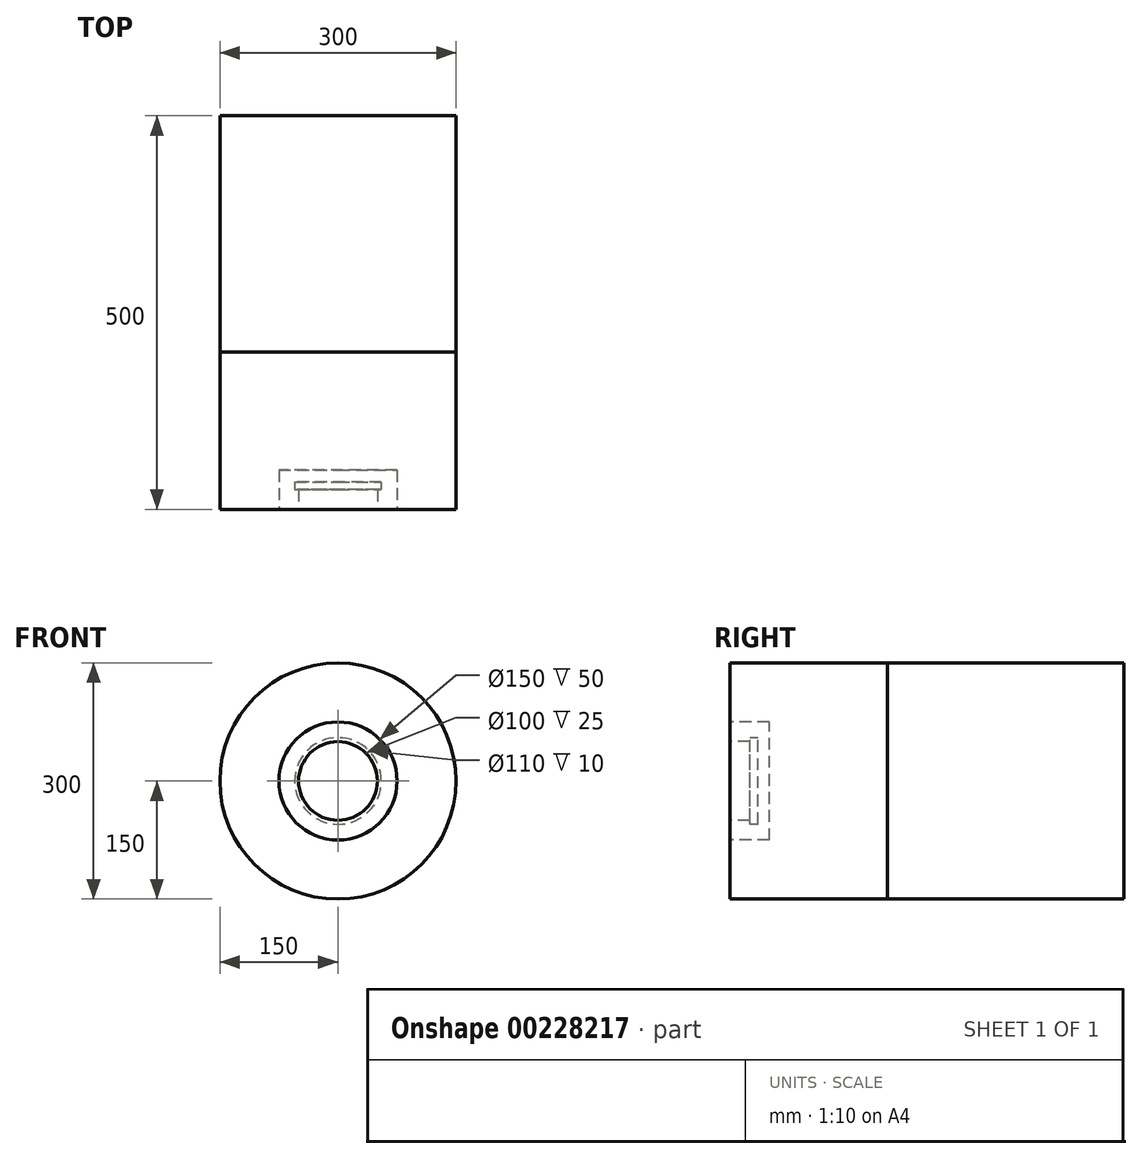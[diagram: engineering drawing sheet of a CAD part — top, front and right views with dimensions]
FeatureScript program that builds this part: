
annotation { "Feature Type Name" : "Feature", "Feature Type Description" : "" }
export const myFeature = defineFeature(function(context is Context, id is Id, definition is map)
    precondition{}
    {
        {
            var Q0;
            Q0=qCreatedBy(makeId("Front.planeOp"),FACE);
            var sketch = newSketch(context, id + "F0", { "sketchPlane" : qUnion([Q0])});
            skCircle(sketch, "E0", {"center": v(0, 0) * mm, "radius": 150 * mm});
            skSolve(sketch);
        }
        {
            var Q0;
            Q0=qCreatedBy(makeId("Front.planeOp"),FACE);
            var sketch = newSketch(context, id + "F1", { "sketchPlane" : qUnion([Q0])});
            skCircle(sketch, "E1", {"center": v(0, 0) * mm, "radius": 75 * mm});
            skSolve(sketch);
        }
        {
            var Q0;
            Q0=qCreatedBy(makeId("Front.planeOp"),FACE);
            var sketch = newSketch(context, id + "F2", { "sketchPlane" : qUnion([Q0])});
            skCircle(sketch, "E2", {"center": v(0, 0) * mm, "radius": 50 * mm});
            skSolve(sketch);
        }
        {
            var Q0;
            Q0 = qSketchRegion(id + "F0", true);
            extrude(context, id + "F3", {"entities" : qUnion([Q0]), "oppositeDirection" : true, "depth" : 200 * mm});
        }
        {
            var Q0;
            Q0=makeQuery(id+"F1.imprint","IMPRINT",FACE,{"disambiguationData":[TD([[makeQuery(id+"F1.imprint","IMPRINT",EDGE,{"derivedFrom":sQuery(id+"F1.wireOp",EDGE,"E1")}),1.0]])]});
            extrude(context, id + "F4", {"entities" : qUnion([Q0]), "operationType" : NewBodyOperationType.REMOVE, "oppositeDirection" : true, "depth" : 50 * mm});
        }
        {
            var Q0;
            Q0 = qSketchRegion(id + "F1", true);
            var Q1;
            Q1=makeQuery(id+"F4.boolean.opBoolean","COPY",FACE,{"derivedFrom":makeQuery(id+"F4.opExtrude","CAP_FACE",FACE,{"disambiguationData":[OSD([sQuery(id+"F1.wireOp",EDGE,"E1")])],"isStart":false})});
            extrude(context, id + "F5", {"entities" : qUnion([Q0]), "endBound" : BoundingType.UP_TO_SURFACE, "oppositeDirection" : true, "endBoundEntityFace" : qUnion([Q1]), "depth" : 25 * mm});
        }
        {
            var Q0;
            Q0 = qSketchRegion(id + "F2", true);
            extrude(context, id + "F6", {"entities" : qUnion([Q0]), "operationType" : NewBodyOperationType.REMOVE, "oppositeDirection" : true, "depth" : 25 * mm});
        }
        {
            var Q0;
            Q0=makeQuery(id+"F6.boolean.opBoolean","COPY",FACE,{"derivedFrom":makeQuery(id+"F6.opExtrude","CAP_FACE",FACE,{"disambiguationData":[OSD([sQuery(id+"F2.wireOp",EDGE,"E2")])],"isStart":false})});
            var sketch = newSketch(context, id + "F7", { "sketchPlane" : qUnion([Q0])});
            skCircle(sketch, "E3", {"center": v(0, 0) * mm, "radius": 55 * mm});
            skSolve(sketch);
        }
        {
            var Q0;
            Q0 = qSketchRegion(id + "F7", true);
            extrude(context, id + "F8", {"entities" : qUnion([Q0]), "operationType" : NewBodyOperationType.REMOVE, "oppositeDirection" : true, "depth" : 10 * mm});
        }
        {
            var Q0;
            Q0 = qSketchRegion(id + "F7", true);
            var Q1;
            Q1=makeQuery(id+"F8.boolean.opBoolean","COPY",FACE,{"derivedFrom":makeQuery(id+"F8.opExtrude","CAP_FACE",FACE,{"disambiguationData":[OSD([sQuery(id+"F7.wireOp",EDGE,"E3")])],"isStart":false})});
            extrude(context, id + "F9", {"entities" : qUnion([Q0]), "endBound" : BoundingType.UP_TO_SURFACE, "oppositeDirection" : true, "endBoundEntityFace" : qUnion([Q1]), "depth" : 25 * mm});
        }
        {
            var Q0;
            Q0=makeQuery(id+"F3.opExtrude","CAP_FACE",FACE,{"disambiguationData":[OSD([sQuery(id+"F0.wireOp",EDGE,"E0")])],"isStart":false});
            var sketch = newSketch(context, id + "F10", { "sketchPlane" : qUnion([Q0])});
            skCircle(sketch, "E4", {"center": v(0, 0) * mm, "radius": 150 * mm});
            skSolve(sketch);
        }
        {
            var Q0;
            Q0 = qSketchRegion(id + "F10", true);
            extrude(context, id + "F11", {"entities" : qUnion([Q0]), "depth" : 300 * mm});
        }
    });
